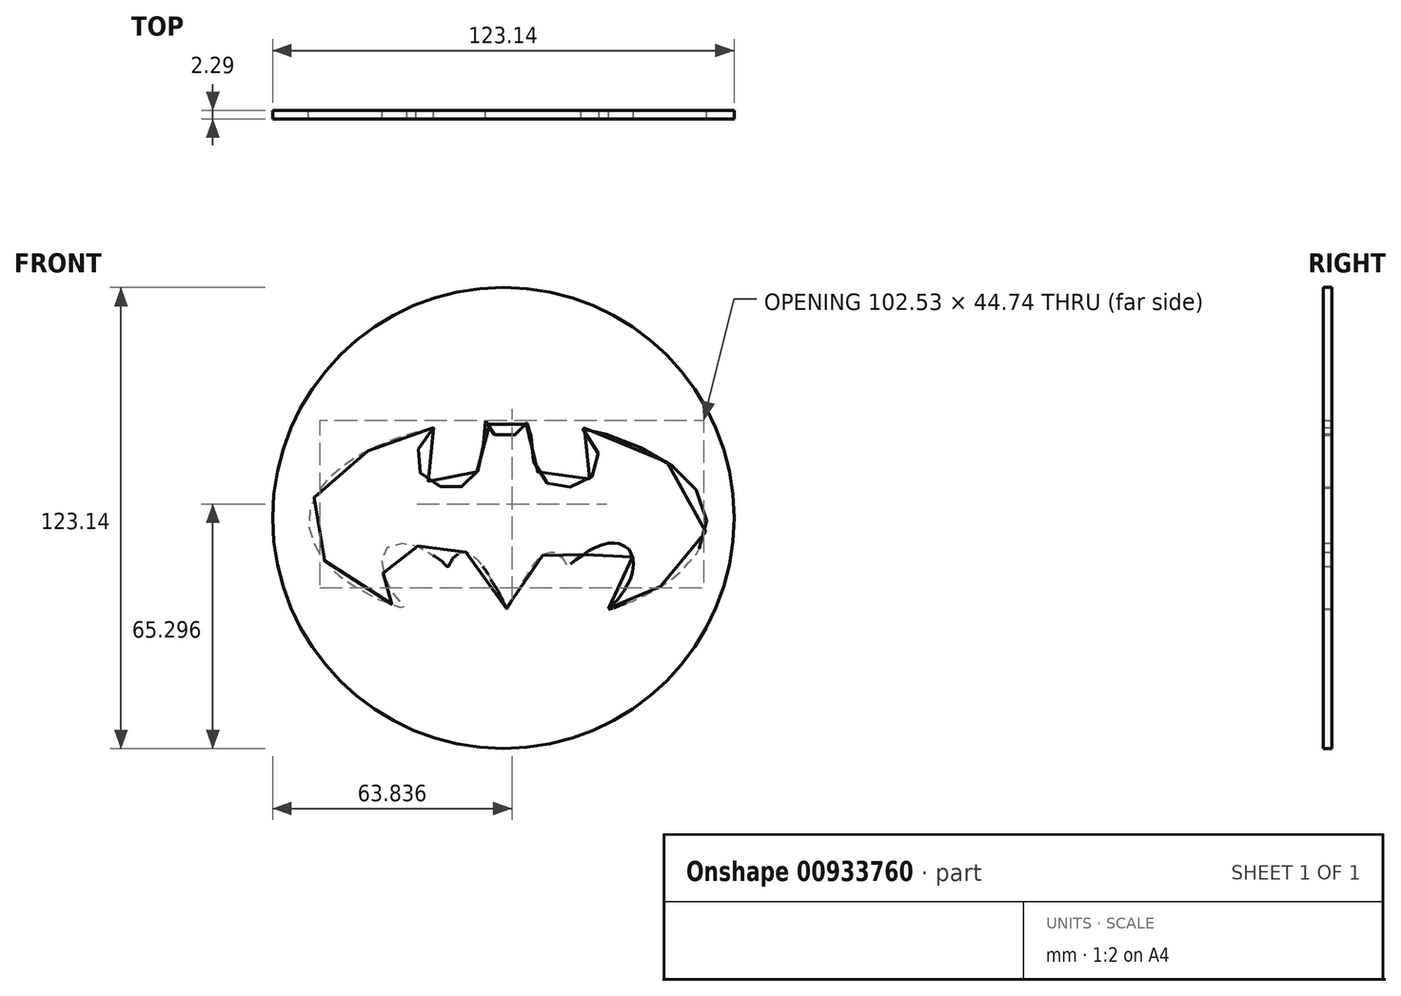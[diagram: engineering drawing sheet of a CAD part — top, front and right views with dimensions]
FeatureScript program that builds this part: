
annotation { "Feature Type Name" : "Feature", "Feature Type Description" : "" }
export const myFeature = defineFeature(function(context is Context, id is Id, definition is map)
    precondition{}
    {
        {
            var Q0;
            Q0=qCreatedBy(makeId("Front.planeOp"),FACE);
            var sketch = newSketch(context, id + "F0", { "sketchPlane" : qUnion([Q0])});
            skCircle(sketch, "E0", {"center": v(0, 0) * mm, "radius": 61.57 * mm});
            skSolve(sketch);
        }
        {
            var Q0;
            Q0=makeQuery(id+"F0.imprint","IMPRINT",FACE,{"disambiguationData":[TD([[makeQuery(id+"F0.imprint","IMPRINT",EDGE,{"derivedFrom":sQuery(id+"F0.wireOp",EDGE,"E0")}),1.0]])]});
            extrude(context, id + "F1", {"entities" : qUnion([Q0]), "depth" : 2.3 * mm, "offsetDistance" : 25.4 * mm});
        }
        {
            var Q0;
            Q0=makeQuery(id+"F1.opExtrude","CAP_FACE",FACE,{"disambiguationData":[OSD([sQuery(id+"F0.wireOp",EDGE,"E0")])],"isStart":false});
            var sketch = newSketch(context, id + "F2", { "sketchPlane" : qUnion([Q0])});
            skFitSpline(sketch, "E1", {"points": [v(-18.62, 24.1) * mm, v(-20.37, 23.68) * mm, v(-22.5, 23.2) * mm, v(-25.63, 22.25) * mm, v(-28.9, 21.1) * mm, v(-30.89, 20.24) * mm, v(-34.07, 19.02) * mm, v(-35.6, 18.3) * mm, v(-38.01, 17) * mm, v(-40.12, 15.72) * mm, v(-42.45, 14.15) * mm, v(-44.04, 12.9) * mm, v(-46.54, 10.74) * mm, v(-48, 9.13) * mm, v(-50.03, 6.33) * mm, v(-51.3, 3.79) * mm, v(-51.78, 1.8) * mm, v(-52.07, -0.31) * mm, v(-51.83, -3.11) * mm, v(-51.15, -5.65) * mm, v(-49.6, -8.66) * mm, v(-48.79, -10.1) * mm, v(-47.27, -12.04) * mm, v(-45.42, -14.04) * mm, v(-42.91, -16.21) * mm, v(-40.12, -18.1) * mm, v(-36.3, -20.28) * mm, v(-32.68, -21.98) * mm, v(-29.87, -23) * mm, v(-26.37, -24.23) * mm, v(-25.96, -24.29) * mm, v(-25.79, -24.2) * mm, v(-26, -24.07) * mm, v(-26.5, -23.56) * mm, v(-27.91, -22.16) * mm, v(-29.77, -19.57) * mm, v(-30.7, -18.1) * mm, v(-31.42, -16.53) * mm, v(-32.13, -14.6) * mm, v(-32.4, -12.05) * mm, v(-32.2, -10.38) * mm, v(-31.92, -9.43) * mm, v(-31.04, -7.92) * mm, v(-29.75, -7.18) * mm, v(-28.23, -6.77) * mm, v(-25.62, -6.78) * mm, v(-23.65, -7.25) * mm, v(-22.59, -7.66) * mm, v(-20.72, -8.68) * mm, v(-18.76, -9.93) * mm, v(-16.3, -11.69) * mm, v(-15.03, -12.92) * mm, v(-14.65, -12.8) * mm, v(-13.75, -11.19) * mm, v(-12.28, -9.73) * mm, v(-10.53, -9.1) * mm, v(-9.05, -9.46) * mm, v(-7.4, -10.78) * mm, v(-5.55, -12.89) * mm, v(-3.88, -15.35) * mm, v(-3.28, -16.6) * mm, v(-1.44, -19.5) * mm, v(-0.27, -21.9) * mm, v(1.1, -24.4) * mm, v(1.37, -24.09) * mm, v(2.28, -22.4) * mm, v(3.7, -19.85) * mm, v(5.45, -16.7) * mm, v(6.38, -15.09) * mm, v(7.9, -12.72) * mm, v(9.44, -10.91) * mm, v(10.92, -9.71) * mm, v(12.4, -9.14) * mm, v(13.45, -9.17) * mm, v(14.36, -9.6) * mm, v(14.55, -9.77) * mm, v(15.56, -10.5) * mm, v(16.46, -11.84) * mm, v(17.05, -12.92) * mm, v(17.41, -12.84) * mm, v(18.64, -11.6) * mm, v(21.12, -9.91) * mm, v(23.15, -8.53) * mm, v(25.11, -7.62) * mm, v(27.89, -6.78) * mm, v(29.47, -6.71) * mm, v(30.7, -6.8) * mm, v(32.38, -7.59) * mm, v(33.47, -8.23) * mm, v(33.9, -9.14) * mm, v(34.37, -10.31) * mm, v(34.7, -11.86) * mm, v(34.43, -14.8) * mm, v(33.58, -16.77) * mm, v(32.54, -18.8) * mm, v(31.7, -20.08) * mm, v(30.76, -21.46) * mm, v(29.57, -22.66) * mm, v(28.61, -23.77) * mm, v(28.04, -24.21) * mm, v(28.15, -24.4) * mm, v(28.66, -24.3) * mm, v(29.4, -24.1) * mm, v(30.68, -23.52) * mm, v(33.34, -22.55) * mm, v(35.09, -21.95) * mm, v(37.17, -20.97) * mm, v(39.09, -20) * mm, v(41.26, -18.74) * mm, v(43.99, -16.97) * mm, v(46.12, -15.38) * mm, v(48.21, -13.44) * mm, v(50.15, -11.14) * mm, v(51.91, -8.84) * mm, v(53.49, -5.24) * mm, v(53.7, -4.89) * mm, v(54.24, -1.84) * mm, v(54.2, 1.27) * mm, v(53.42, 4.5) * mm, v(50.97, 8.1) * mm, v(49.47, 10.08) * mm, v(46, 13.17) * mm, v(41.85, 16.09) * mm, v(37.73, 18.28) * mm, v(35.26, 19.44) * mm, v(30.68, 21.34) * mm, v(26.16, 22.82) * mm, v(22.23, 23.95) * mm, v(20.73, 24.06) * mm, v(21.04, 23.85) * mm, v(22.25, 22.27) * mm, v(23.1, 21.44) * mm, v(25.03, 17.9) * mm, v(25.51, 15.12) * mm, v(24.97, 12.7) * mm, v(24.2, 11.71) * mm, v(22.8, 10.3) * mm, v(21.45, 9.48) * mm, v(19.76, 8.67) * mm, v(17.3, 8.16) * mm, v(14.9, 8.1) * mm, v(13.47, 8.42) * mm, v(12.2, 8.9) * mm, v(10.62, 10.36) * mm, v(9.5, 11.79) * mm, v(8.37, 14) * mm, v(7.89, 16.32) * mm, v(7.75, 17.57) * mm, v(7.64, 20.2) * mm, v(7.33, 22.62) * mm, v(7.1, 24.83) * mm, v(6.91, 25.75) * mm, v(6.7, 26) * mm, v(6.4, 25.87) * mm, v(6.13, 25.06) * mm, v(5.42, 23.72) * mm, v(4.65, 22.35) * mm, v(4.21, 22.06) * mm, v(3.26, 22.2) * mm, v(1.7, 22.33) * mm, v(0.24, 22.42) * mm, v(-1.56, 22.18) * mm, v(-2.33, 22.2) * mm, v(-2.77, 23) * mm, v(-3.34, 24.47) * mm, v(-4.1, 25.7) * mm, v(-4.47, 26.1) * mm, v(-4.74, 25.9) * mm, v(-4.77, 25.3) * mm, v(-4.98, 23.61) * mm, v(-5.16, 22.3) * mm, v(-5.35, 19.15) * mm, v(-5.56, 16.6) * mm, v(-6.11, 14.09) * mm, v(-7.07, 12.27) * mm, v(-8.24, 10.47) * mm, v(-9.67, 9.07) * mm, v(-10.65, 8.5) * mm, v(-11.72, 8.25) * mm, v(-12.9, 8.12) * mm, v(-14.28, 8.23) * mm, v(-16.3, 8.3) * mm, v(-18.07, 8.92) * mm, v(-20.15, 9.9) * mm, v(-21.55, 11.2) * mm, v(-22.71, 12.84) * mm, v(-23.27, 14.53) * mm, v(-23.33, 16.19) * mm, v(-22.64, 18.66) * mm, v(-21.36, 20.82) * mm, v(-19.67, 22.8) * mm, v(-18.62, 24.1) * mm]});
            skSolve(sketch);
        }
        {
            var Q0;
            Q0=makeQuery(id+"F2.imprint","IMPRINT",FACE,{"disambiguationData":[TD([[makeQuery(id+"F2.imprint","IMPRINT",EDGE,{"derivedFrom":sQuery(id+"F2.wireOp",EDGE,"E1")}),1.0]])]});
            extrude(context, id + "F3", {"entities" : qUnion([Q0]), "operationType" : NewBodyOperationType.REMOVE, "oppositeDirection" : true, "depth" : 25.4 * mm, "offsetDistance" : 25.4 * mm, "hasSecondDirection" : true, "secondDirectionOppositeDirection" : false, "secondDirectionDepth" : 25.4 * mm});
        }
    });
